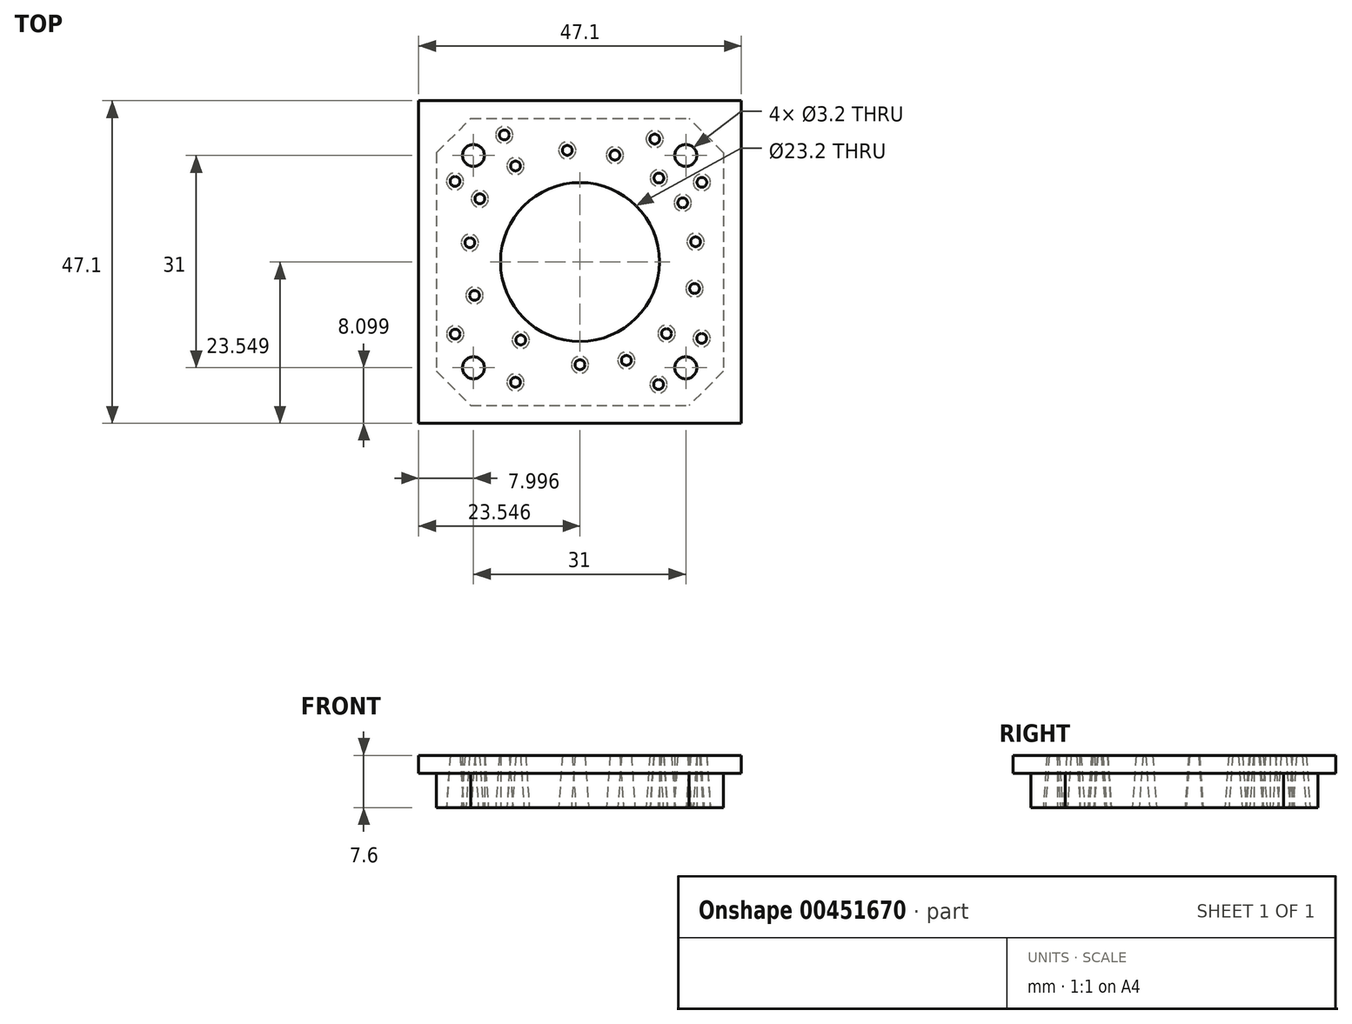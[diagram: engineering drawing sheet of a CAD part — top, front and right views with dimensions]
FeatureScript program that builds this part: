
annotation { "Feature Type Name" : "Feature", "Feature Type Description" : "" }
export const myFeature = defineFeature(function(context is Context, id is Id, definition is map)
    precondition{}
    {
        {
            var Q0;
            Q0=qCreatedBy(makeId("Top.planeOp"),FACE);
            var sketch = newSketch(context, id + "F0", { "sketchPlane" : qUnion([Q0])});
            skLineSegment(sketch, "E0.bottom", {"start": v(-41.82, 29.14) * mm, "end": v(0.08, 29.14) * mm});
            skLineSegment(sketch, "E0.top", {"start": v(-41.82, -12.76) * mm, "end": v(0.08, -12.76) * mm});
            skLineSegment(sketch, "E0.left", {"start": v(-41.82, 29.14) * mm, "end": v(-41.82, -12.76) * mm});
            skLineSegment(sketch, "E0.right", {"start": v(0.08, 29.14) * mm, "end": v(0.08, -12.76) * mm});
            skLineSegment(sketch, "E1", {"start": v(-41.82, 29.14) * mm, "end": v(0.08, -12.76) * mm, "construction": true});
            skCircle(sketch, "E2", {"center": v(-20.87, 8.19) * mm, "radius": 11.6 * mm});
            skLineSegment(sketch, "E3.bottom", {"start": v(-36.42, -7.26) * mm, "end": v(-5.42, -7.26) * mm, "construction": true});
            skLineSegment(sketch, "E3.top", {"start": v(-36.42, 23.74) * mm, "end": v(-5.42, 23.74) * mm, "construction": true});
            skLineSegment(sketch, "E3.left", {"start": v(-36.42, -7.26) * mm, "end": v(-36.42, 23.74) * mm, "construction": true});
            skLineSegment(sketch, "E3.right", {"start": v(-5.42, -7.26) * mm, "end": v(-5.42, 23.74) * mm, "construction": true});
            skCircle(sketch, "E4", {"center": v(-36.42, 23.74) * mm, "radius": 1.6 * mm});
            skCircle(sketch, "E5", {"center": v(-5.42, 23.74) * mm, "radius": 1.6 * mm});
            skCircle(sketch, "E6", {"center": v(-5.42, -7.26) * mm, "radius": 1.6 * mm});
            skCircle(sketch, "E7", {"center": v(-36.42, -7.26) * mm, "radius": 1.6 * mm});
            skSolve(sketch);
        }
        {
            var Q0;
            Q0=makeQuery(id+"F0.imprint","IMPRINT",FACE,{"disambiguationData":[TD([[makeQuery(id+"F0.imprint","IMPRINT",EDGE,{"derivedFrom":sQuery(id+"F0.wireOp",EDGE,"E0.bottom")}),-1.0]])]});
            extrude(context, id + "F1", {"entities" : qUnion([Q0]), "depth" : 5 * mm});
        }
        {
            var Q0;
            Q0=makeQuery(id+"F1.opExtrude","SWEPT_EDGE",EDGE,{"disambiguationData":[OSD([sQuery(id+"F0.wireOp",EDGE,"E0.top"),sQuery(id+"F0.wireOp",EDGE,"E0.left")])]});
            var Q1;
            Q1=makeQuery(id+"F1.opExtrude","SWEPT_EDGE",EDGE,{"disambiguationData":[OSD([sQuery(id+"F0.wireOp",EDGE,"E0.top"),sQuery(id+"F0.wireOp",EDGE,"E0.right")])]});
            var Q2;
            Q2=makeQuery(id+"F1.opExtrude","SWEPT_EDGE",EDGE,{"disambiguationData":[OSD([sQuery(id+"F0.wireOp",EDGE,"E0.bottom"),sQuery(id+"F0.wireOp",EDGE,"E0.left")])]});
            var Q3;
            Q3=makeQuery(id+"F1.opExtrude","SWEPT_EDGE",EDGE,{"disambiguationData":[OSD([sQuery(id+"F0.wireOp",EDGE,"E0.bottom"),sQuery(id+"F0.wireOp",EDGE,"E0.right")])]});
            chamfer(context, id + "F2", {"entities" : qUnion([Q0, Q1, Q2, Q3]), "width" : 5 * mm, "tangentPropagation" : true});
        }
        {
            var Q0;
            Q0=makeQuery(id+"F1.opExtrude","CAP_FACE",FACE,{"disambiguationData":[OSD([sQuery(id+"F0.wireOp",EDGE,"E0.bottom"),sQuery(id+"F0.wireOp",EDGE,"E0.top"),sQuery(id+"F0.wireOp",EDGE,"E0.left"),sQuery(id+"F0.wireOp",EDGE,"E0.right"),sQuery(id+"F0.wireOp",EDGE,"E2"),sQuery(id+"F0.wireOp",EDGE,"E4"),sQuery(id+"F0.wireOp",EDGE,"E5"),sQuery(id+"F0.wireOp",EDGE,"E6"),sQuery(id+"F0.wireOp",EDGE,"E7")])],"isStart":false});
            var sketch = newSketch(context, id + "F3", { "sketchPlane" : qUnion([Q0])});
            skCircle(sketch, "E8.0", {"center": v(-5.42, 23.74) * mm, "radius": 1.6 * mm});
            skCircle(sketch, "E8.1", {"center": v(-36.42, 23.74) * mm, "radius": 1.6 * mm});
            skCircle(sketch, "E8.2", {"center": v(-36.42, -7.26) * mm, "radius": 1.6 * mm});
            skCircle(sketch, "E8.3", {"center": v(-5.42, -7.26) * mm, "radius": 1.6 * mm});
            skCircle(sketch, "E8.4", {"center": v(-20.87, 8.19) * mm, "radius": 11.6 * mm});
            skLineSegment(sketch, "E9.0", {"start": v(-41.82, 29.14) * mm, "end": v(0.08, 29.14) * mm, "construction": true});
            skLineSegment(sketch, "E9.1", {"start": v(-41.82, 29.14) * mm, "end": v(-41.82, -12.76) * mm, "construction": true});
            skLineSegment(sketch, "E9.2", {"start": v(0.08, 29.14) * mm, "end": v(0.08, -12.76) * mm, "construction": true});
            skLineSegment(sketch, "E9.3", {"start": v(-41.82, -12.76) * mm, "end": v(0.08, -12.76) * mm, "construction": true});
            skLineSegment(sketch, "E10.0", {"start": v(-44.42, 31.74) * mm, "end": v(2.68, 31.74) * mm});
            skLineSegment(sketch, "E10.1", {"start": v(-44.42, 31.74) * mm, "end": v(-44.42, -15.36) * mm});
            skLineSegment(sketch, "E10.2", {"start": v(-44.42, -15.36) * mm, "end": v(2.68, -15.36) * mm});
            skLineSegment(sketch, "E10.3", {"start": v(2.68, 31.74) * mm, "end": v(2.68, -15.36) * mm});
            skSolve(sketch);
        }
        {
            var Q0;
            Q0=makeQuery(id+"F3.imprint","IMPRINT",FACE,{"disambiguationData":[TD([[makeQuery(id+"F3.imprint","IMPRINT",EDGE,{"derivedFrom":sQuery(id+"F3.wireOp",EDGE,"E10.0")}),-1.0]])]});
            var Q1;
            Q1=makeQuery(id+"F3.imprint","IMPRINT",FACE,{"disambiguationData":[TD([[makeQuery(id+"F3.imprint","IMPRINT",EDGE,{"derivedFrom":sQuery(id+"F3.wireOp",EDGE,"E8.0")}),-1.0]])]});
            extrude(context, id + "F4", {"entities" : qUnion([Q0, Q1]), "operationType" : NewBodyOperationType.ADD, "depth" : 2.6 * mm});
        }
        {
            var Q0;
            Q0=makeQuery(id+"F1.opExtrude","CAP_FACE",FACE,{"disambiguationData":[OSD([sQuery(id+"F0.wireOp",EDGE,"E0.bottom"),sQuery(id+"F0.wireOp",EDGE,"E0.top"),sQuery(id+"F0.wireOp",EDGE,"E0.left"),sQuery(id+"F0.wireOp",EDGE,"E0.right"),sQuery(id+"F0.wireOp",EDGE,"E2"),sQuery(id+"F0.wireOp",EDGE,"E4"),sQuery(id+"F0.wireOp",EDGE,"E5"),sQuery(id+"F0.wireOp",EDGE,"E6"),sQuery(id+"F0.wireOp",EDGE,"E7")])],"isStart":true});
            var sketch = newSketch(context, id + "F5", { "sketchPlane" : qUnion([Q0])});
            skCircle(sketch, "E11", {"center": v(-20.87, 6.81) * mm, "radius": 1.25 * mm});
            skCircle(sketch, "E12", {"center": v(-29.52, 3.2) * mm, "radius": 1.25 * mm});
            skCircle(sketch, "E13", {"center": v(-36.27, -3.3) * mm, "radius": 1.25 * mm});
            skCircle(sketch, "E14", {"center": v(-36.95, -11.01) * mm, "radius": 1.25 * mm});
            skCircle(sketch, "E15", {"center": v(-35.5, -17.43) * mm, "radius": 1.25 * mm});
            skCircle(sketch, "E16", {"center": v(-30.3, -22.21) * mm, "radius": 1.25 * mm});
            skCircle(sketch, "E17", {"center": v(-22.73, -24.5) * mm, "radius": 1.25 * mm});
            skCircle(sketch, "E18", {"center": v(-15.77, -23.8) * mm, "radius": 1.25 * mm});
            skCircle(sketch, "E19", {"center": v(-9.36, -20.45) * mm, "radius": 1.25 * mm});
            skCircle(sketch, "E20", {"center": v(-5.88, -16.83) * mm, "radius": 1.25 * mm});
            skCircle(sketch, "E21", {"center": v(-4, -11.14) * mm, "radius": 1.25 * mm});
            skCircle(sketch, "E22", {"center": v(-4.15, -4.31) * mm, "radius": 1.25 * mm});
            skCircle(sketch, "E23", {"center": v(-8.23, 2.26) * mm, "radius": 1.25 * mm});
            skCircle(sketch, "E24", {"center": v(-14.1, 6.18) * mm, "radius": 1.25 * mm});
            skCircle(sketch, "E25", {"center": v(-9.4, 9.7) * mm, "radius": 1.25 * mm});
            skCircle(sketch, "E26", {"center": v(-30.3, 9.37) * mm, "radius": 1.25 * mm});
            skCircle(sketch, "E27", {"center": v(-39.1, 2.33) * mm, "radius": 1.25 * mm});
            skCircle(sketch, "E28", {"center": v(-39.12, -19.96) * mm, "radius": 1.25 * mm});
            skCircle(sketch, "E29", {"center": v(-31.92, -26.74) * mm, "radius": 1.25 * mm});
            skCircle(sketch, "E30", {"center": v(-9.96, -26.14) * mm, "radius": 1.25 * mm});
            skCircle(sketch, "E31", {"center": v(-3.08, -19.81) * mm, "radius": 1.25 * mm});
            skCircle(sketch, "E32", {"center": v(-3.1, 2.96) * mm, "radius": 1.25 * mm});
            skSolve(sketch);
        }
        {
            var Q0;
            Q0 = qSketchRegion(id + "F5", true);
            extrude(context, id + "F6", {"entities" : qUnion([Q0]), "operationType" : NewBodyOperationType.REMOVE, "oppositeDirection" : true, "depth" : 25 * mm, "hasDraft" : true, "draftAngle" : 4 * degree, "draftPullDirection" : true});
        }
    });
